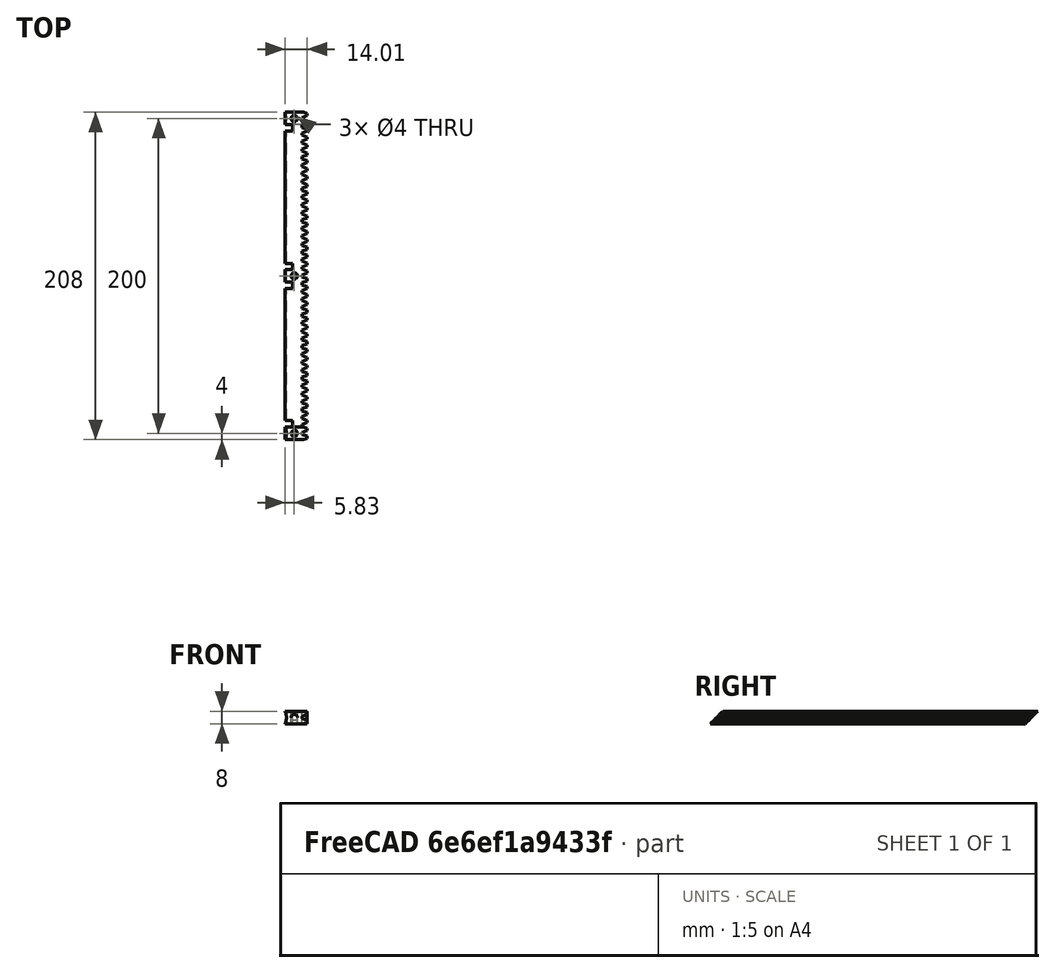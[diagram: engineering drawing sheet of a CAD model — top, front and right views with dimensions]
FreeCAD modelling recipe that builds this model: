
FCSTD DOCUMENT  (FreeCAD 0.17R13522 (Git))
Label: rack
License: All rights reserved
LicenseURL: http://en.wikipedia.org/wiki/All_rights_reserved
objects: Part::Box×7, Part::Cylinder×4, Part::MultiFuse×2, Part::FeaturePython×1, Part::Cut×1
note: 15 computed .brp shape members not serialized (recipe doc carries the construction recipe); baked Part::Feature solids carry a one-line shape summary decoded from their .brp

FEATURE [Part::FeaturePython] InvoluteRack  # WARN: FeaturePython — macro-defined, semantics opaque (R4)
  Placement = pos=(11.5915,2.5,-4) rot=(0,0,1;0rad)
  beta = 0
  double_helix = false
  head = 0
  height = 8
  module = 1.59155
  pressure_angle = 20
  teeth = 42
  thickness = 1
  expr: Placement.Base.x = 10 + 5 / pi
  expr: module = 5 / pi
FEATURE [Part::Box] Box  label="Cube"
  AttacherType = Attacher::AttachEngine3D
  Height = 8
  Length = 12
  Placement = pos=(-2,0,-4) rot=(0,0,1;0rad)
  Width = 210
FEATURE [Part::Cylinder] Cylinder
  Angle = 360
  AttacherType = Attacher::AttachEngine3D
  Height = 10
  Placement = pos=(5,5,-5) rot=(0,0,1;0rad)
  Radius = 2
FEATURE [Part::Cylinder] Cylinder001
  Angle = 360
  AttacherType = Attacher::AttachEngine3D
  Height = 10
  Placement = pos=(5,105,-5) rot=(0,0,1;0rad)
  Radius = 2
FEATURE [Part::Cylinder] Cylinder002
  Angle = 360
  AttacherType = Attacher::AttachEngine3D
  Height = 10
  Placement = pos=(5,205,-5) rot=(0,0,1;0rad)
  Radius = 2
FEATURE [Part::MultiFuse] Fusion  label="Positive Fusion"
  Shapes = -> [Box,InvoluteRack]
FEATURE [Part::Cylinder] Cylinder003  label="Rail"
  Angle = 360
  AttacherType = Attacher::AttachEngine3D
  Height = 210
  Placement = pos=(-10,0,0) rot=(-1,0,0;1.5708rad)
  Radius = 10
FEATURE [Part::Box] Box001  label="Cube001"
  AttacherType = Attacher::AttachEngine3D
  Height = 20
  Length = 20
  Placement = pos=(-5,10,5) rot=(1,0,0;2.35619rad)
  Width = 10
FEATURE [Part::Box] Box002  label="Cube002"
  AttacherType = Attacher::AttachEngine3D
  Height = 20
  Length = 20
  Placement = pos=(-5,200,-5) rot=(-1,0,0;0.785398rad)
  Width = 10
FEATURE [Part::Box] Box003  label="Cube003"
  AttacherType = Attacher::AttachEngine3D
  Height = 8
  Length = 5
  Placement = pos=(-1,97,-4) rot=(0,0,1;0rad)
  Width = 4
FEATURE [Part::Box] Box004  label="Cube004"
  AttacherType = Attacher::AttachEngine3D
  Height = 8
  Length = 5
  Placement = pos=(-1,109,-4) rot=(0,0,1;0rad)
  Width = 4
FEATURE [Part::Box] Box005  label="Cube005"
  AttacherType = Attacher::AttachEngine3D
  Height = 8
  Length = 5
  Placement = pos=(-1,197,-4) rot=(0,0,1;0rad)
  Width = 4
FEATURE [Part::Box] Box006  label="Cube006"
  AttacherType = Attacher::AttachEngine3D
  Height = 8
  Length = 5
  Placement = pos=(-1,9,-4) rot=(0,0,1;0rad)
  Width = 4
FEATURE [Part::MultiFuse] Fusion001  label="Negative Fusion"
  Shapes = -> [Cylinder,Cylinder001,Cylinder002,Cylinder003,Box001,Box002,Box003,Box004,Box005,Box006]
FEATURE [Part::Cut] Cut
  Base = -> Fusion
  Tool = -> Fusion001
